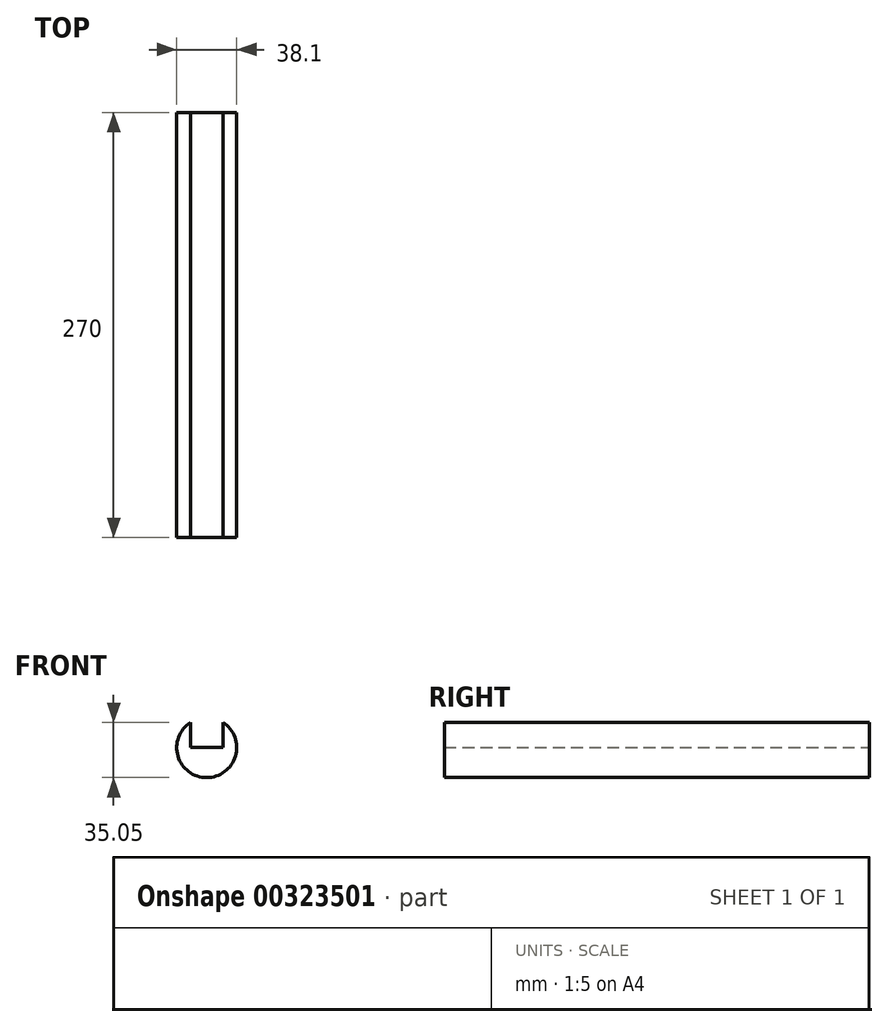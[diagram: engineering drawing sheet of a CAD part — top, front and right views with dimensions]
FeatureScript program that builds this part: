
annotation { "Feature Type Name" : "Feature", "Feature Type Description" : "" }
export const myFeature = defineFeature(function(context is Context, id is Id, definition is map)
    precondition{}
    {
        {
            var Q0;
            Q0=qCreatedBy(makeId("Front.planeOp"),FACE);
            var sketch = newSketch(context, id + "F0", { "sketchPlane" : qUnion([Q0])});
            skCircle(sketch, "E0", {"center": v(0, 0) * mm, "radius": 19.05 * mm});
            skSolve(sketch);
        }
        {
            var Q0;
            Q0=makeQuery(id+"F0.imprint","IMPRINT",FACE,{"disambiguationData":[TD([[makeQuery(id+"F0.imprint","IMPRINT",EDGE,{"derivedFrom":sQuery(id+"F0.wireOp",EDGE,"E0")}),1.0]])]});
            extrude(context, id + "F1", {"entities" : qUnion([Q0]), "depth" : 270 * mm});
        }
        {
            var Q0;
            Q0=qCreatedBy(makeId("Front.planeOp"),FACE);
            var sketch = newSketch(context, id + "F2", { "sketchPlane" : qUnion([Q0])});
            skLineSegment(sketch, "E1.bottom", {"start": v(0, 0) * mm, "end": v(-10.33, 0) * mm});
            skLineSegment(sketch, "E1.top", {"start": v(0, 24.2) * mm, "end": v(-10.33, 24.2) * mm});
            skLineSegment(sketch, "E1.left", {"start": v(0, 0) * mm, "end": v(0, 24.2) * mm});
            skLineSegment(sketch, "E1.right", {"start": v(-10.33, 0) * mm, "end": v(-10.33, 24.2) * mm});
            skLineSegment(sketch, "E2.MirrorCS", {"start": v(0, 24.2) * mm, "end": v(10.33, 24.2) * mm});
            skLineSegment(sketch, "E3.MirrorCS", {"start": v(0, 0) * mm, "end": v(10.33, 0) * mm});
            skLineSegment(sketch, "E4.MirrorCS", {"start": v(10.33, 0) * mm, "end": v(10.33, 24.2) * mm});
            skSolve(sketch);
        }
        {
            var Q0;
            Q0 = qSketchRegion(id + "F2", true);
            extrude(context, id + "F3", {"entities" : qUnion([Q0]), "operationType" : NewBodyOperationType.REMOVE, "depth" : 279.15 * mm});
        }
    });
